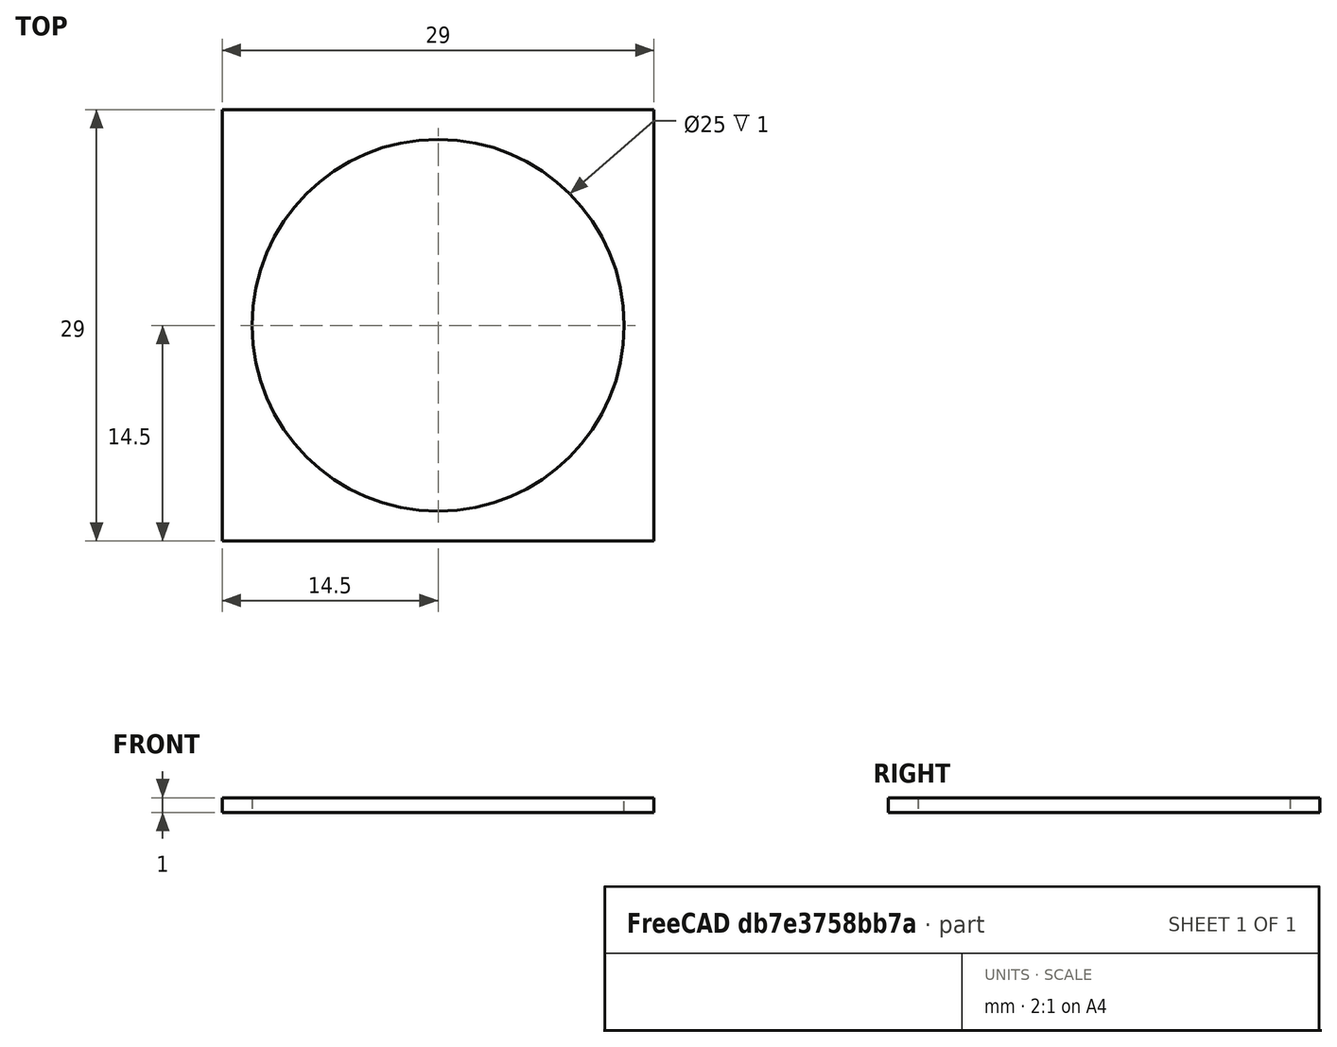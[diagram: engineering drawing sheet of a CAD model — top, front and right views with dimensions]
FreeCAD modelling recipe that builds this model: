
FCSTD DOCUMENT  (FreeCAD 0.20R29603 (Git))
Label: SlotTest
License: All rights reserved
LicenseURL: http://en.wikipedia.org/wiki/All_rights_reserved
objects: Sketcher::SketchObject×1, PartDesign::Pad×1, PartDesign::Body×1
note: 4 computed .brp shape members not serialized (recipe doc carries the construction recipe); baked Part::Feature solids carry a one-line shape summary decoded from their .brp

FEATURE [Sketcher::SketchObject] Sketch
  FullyConstrained = true
  MapMode = 5
  Support = -> [XY_Plane]
  sketch-geometry (6):
    g0: LineSegment StartX=-14.5 StartY=14.5 StartZ=0 EndX=-14.5 EndY=-14.5 EndZ=0
    g1: LineSegment StartX=-14.5 StartY=-14.5 StartZ=0 EndX=14.5 EndY=-14.5 EndZ=0
    g2: LineSegment StartX=14.5 StartY=-14.5 StartZ=0 EndX=14.5 EndY=14.5 EndZ=0
    g3: LineSegment StartX=14.5 StartY=14.5 StartZ=0 EndX=-14.5 EndY=14.5 EndZ=0
    g4: GeomPoint X=0 Y=0 Z=0
    g5: Circle CenterX=0 CenterY=0 CenterZ=0 NormalX=0 NormalY=0 NormalZ=1 AngleXU=0 Radius=12.5
  constraints (14):
    c: Coincident(g0,g1)
    c: Coincident(g1,g2)
    c: Coincident(g2,g3)
    c: Coincident(g3,g0)
    c: Horizontal(g1)
    c: Horizontal(g3)
    c: Vertical(g0)
    c: Vertical(g2)
    c: Symmetric(g1,g0,g4)
    c: Coincident(g4,g-1)
    c: DistanceX(g3,g3) = 29
    c: DistanceY(g0,g0) = 29
    c: Coincident(g5,g4)
    c: Diameter(g5) = 25
FEATURE [PartDesign::Pad] Pad
  Direction = (0,0,1)
  Length = 1
  Length2 = 10
  Profile = -> Sketch
  ReferenceAxis = -> Sketch [N_Axis]
  Type = 0
FEATURE [PartDesign::Body] Body
  Group = -> [Sketch,Pad]
  Origin = -> Origin
  Tip = -> Pad
